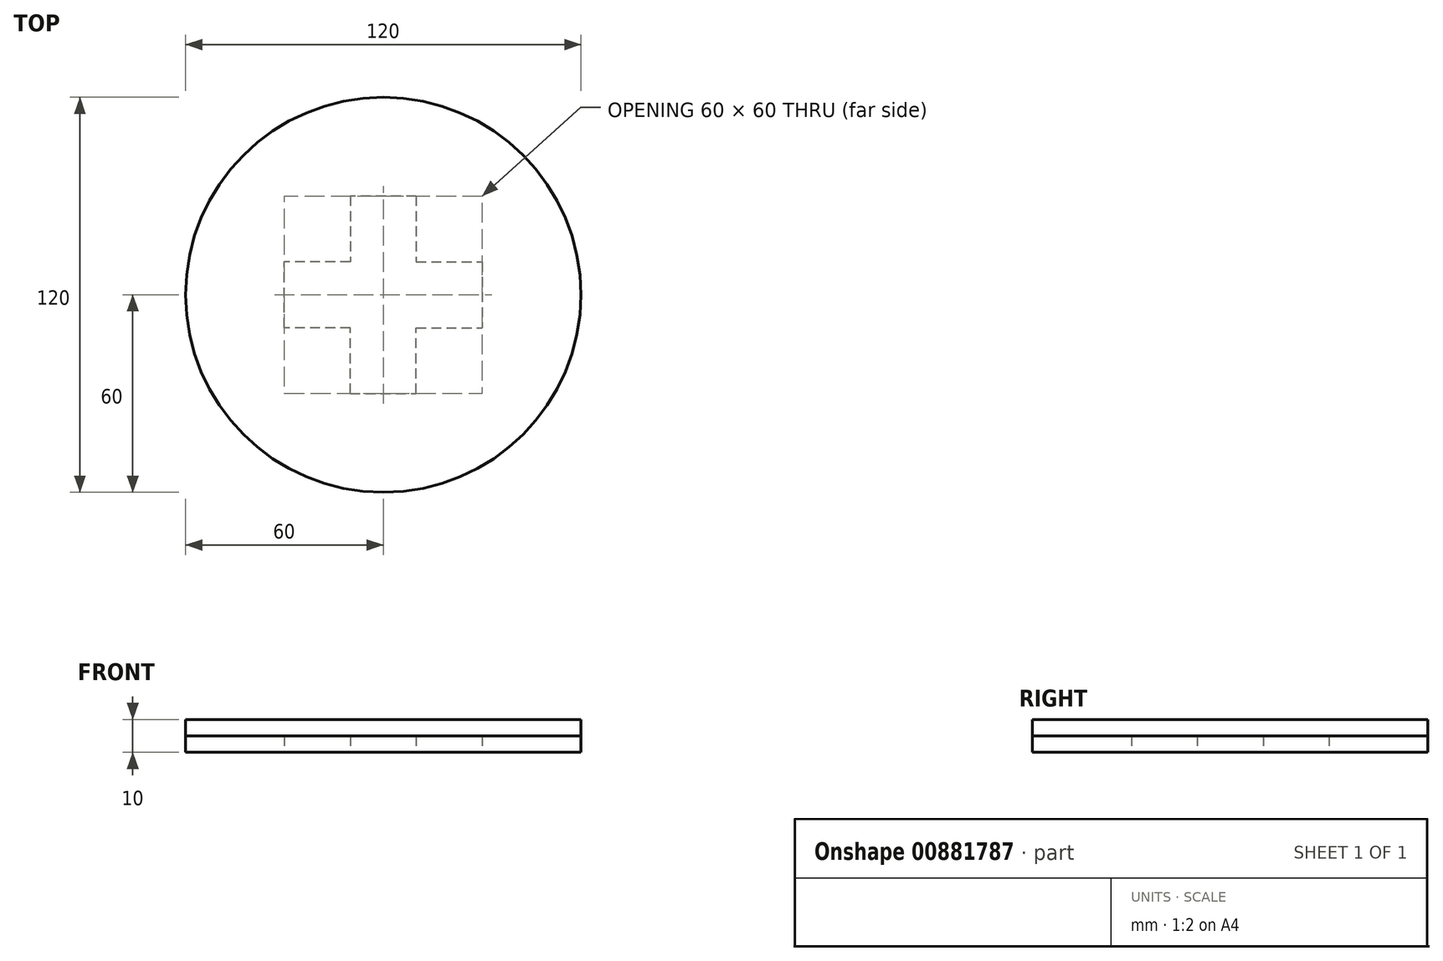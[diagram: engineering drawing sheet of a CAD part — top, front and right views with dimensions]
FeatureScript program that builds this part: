
annotation { "Feature Type Name" : "Feature", "Feature Type Description" : "" }
export const myFeature = defineFeature(function(context is Context, id is Id, definition is map)
    precondition{}
    {
        {
            var Q0;
            Q0=qCreatedBy(makeId("Top.planeOp"),FACE);
            var sketch = newSketch(context, id + "F0", { "sketchPlane" : qUnion([Q0])});
            skCircle(sketch, "E0", {"center": v(0, 0) * mm, "radius": 60 * mm});
            skLineSegment(sketch, "E1", {"start": v(0, 0) * mm, "end": v(-37.32, 0) * mm, "construction": true});
            skLineSegment(sketch, "E2", {"start": v(0, 0) * mm, "end": v(0, 42.9) * mm, "construction": true});
            skLineSegment(sketch, "E3", {"start": v(0, 30) * mm, "end": v(-10, 30) * mm});
            skLineSegment(sketch, "E4", {"start": v(-10, 30) * mm, "end": v(-10, 10) * mm});
            skLineSegment(sketch, "E5", {"start": v(-10, 10) * mm, "end": v(-30, 10) * mm});
            skLineSegment(sketch, "E6", {"start": v(-30, 10) * mm, "end": v(-30, 0) * mm});
            skLineSegment(sketch, "E7.MirrorCS", {"start": v(-30, -10) * mm, "end": v(-30, 0) * mm});
            skLineSegment(sketch, "E8.MirrorCS", {"start": v(-10, -10) * mm, "end": v(-30, -10) * mm});
            skLineSegment(sketch, "E9.MirrorCS", {"start": v(-10, -30) * mm, "end": v(-10, -10) * mm});
            skLineSegment(sketch, "E10.MirrorCS", {"start": v(0, -30) * mm, "end": v(-10, -30) * mm});
            skLineSegment(sketch, "E11.MirrorCS", {"start": v(0, 30) * mm, "end": v(10, 30) * mm});
            skLineSegment(sketch, "E12.MirrorCS", {"start": v(10, 30) * mm, "end": v(10, 10) * mm});
            skLineSegment(sketch, "E13.MirrorCS", {"start": v(10, 10) * mm, "end": v(30, 10) * mm});
            skLineSegment(sketch, "E14.MirrorCS", {"start": v(30, 10) * mm, "end": v(30, 0) * mm});
            skLineSegment(sketch, "E15.MirrorCS", {"start": v(30, -10) * mm, "end": v(30, 0) * mm});
            skLineSegment(sketch, "E16.MirrorCS", {"start": v(10, -10) * mm, "end": v(30, -10) * mm});
            skLineSegment(sketch, "E17.MirrorCS", {"start": v(10, -30) * mm, "end": v(10, -10) * mm});
            skLineSegment(sketch, "E18.MirrorCS", {"start": v(0, -30) * mm, "end": v(10, -30) * mm});
            skSolve(sketch);
        }
        {
            var Q0;
            Q0=qSketchRegion(id+"F0",true);
            extrude(context, id + "F1", {"entities" : qUnion([Q0]), "depth" : 5 * mm, "offsetDistance" : 25 * mm});
        }
        {
            var Q0;
            Q0=makeQuery(id+"F1.opExtrude","CAP_FACE",FACE,{"disambiguationData":[OSD([sQuery(id+"F0.wireOp",EDGE,"E0"),sQuery(id+"F0.wireOp",EDGE,"E3"),sQuery(id+"F0.wireOp",EDGE,"E4"),sQuery(id+"F0.wireOp",EDGE,"E5"),sQuery(id+"F0.wireOp",EDGE,"E6"),sQuery(id+"F0.wireOp",EDGE,"E7.MirrorCS"),sQuery(id+"F0.wireOp",EDGE,"E8.MirrorCS"),sQuery(id+"F0.wireOp",EDGE,"E9.MirrorCS"),sQuery(id+"F0.wireOp",EDGE,"E10.MirrorCS"),sQuery(id+"F0.wireOp",EDGE,"E11.MirrorCS"),sQuery(id+"F0.wireOp",EDGE,"E12.MirrorCS"),sQuery(id+"F0.wireOp",EDGE,"E13.MirrorCS"),sQuery(id+"F0.wireOp",EDGE,"E14.MirrorCS"),sQuery(id+"F0.wireOp",EDGE,"E15.MirrorCS"),sQuery(id+"F0.wireOp",EDGE,"E16.MirrorCS"),sQuery(id+"F0.wireOp",EDGE,"E17.MirrorCS"),sQuery(id+"F0.wireOp",EDGE,"E18.MirrorCS")])],"isStart":false});
            var sketch = newSketch(context, id + "F2", { "sketchPlane" : qUnion([Q0])});
            skCircle(sketch, "E19", {"center": v(0, 0) * mm, "radius": 60 * mm});
            skSolve(sketch);
        }
        {
            var Q0;
            Q0=qSketchRegion(id+"F2",true);
            extrude(context, id + "F3", {"entities" : qUnion([Q0]), "depth" : 5 * mm, "offsetDistance" : 25 * mm});
        }
    });
